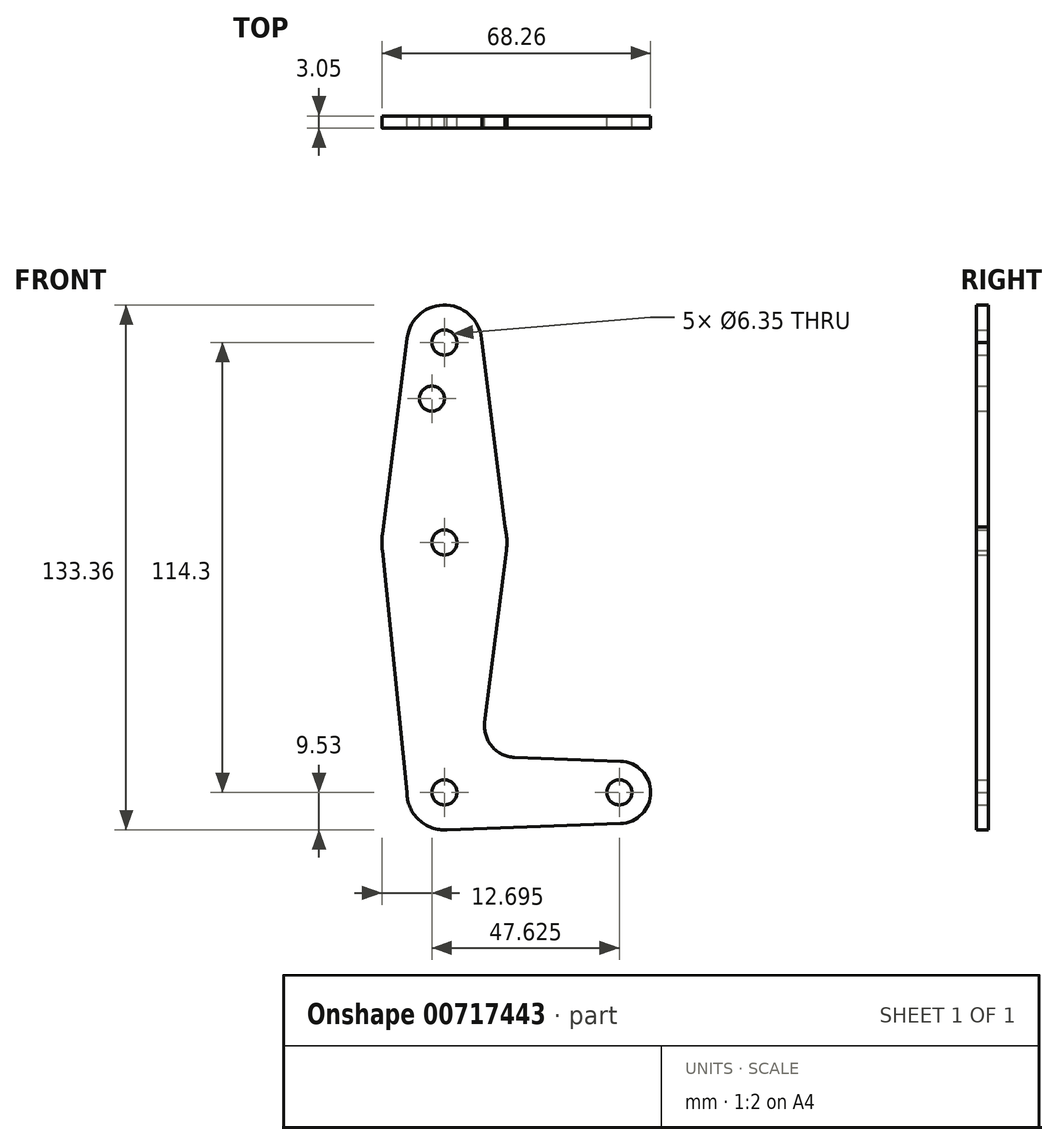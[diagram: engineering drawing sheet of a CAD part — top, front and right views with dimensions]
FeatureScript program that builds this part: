
annotation { "Feature Type Name" : "Feature", "Feature Type Description" : "" }
export const myFeature = defineFeature(function(context is Context, id is Id, definition is map)
    precondition{}
    {
        {
            var Q0;
            Q0=qCreatedBy(makeId("Front.planeOp"),FACE);
            var sketch = newSketch(context, id + "F0", { "sketchPlane" : qUnion([Q0])});
            skLineSegment(sketch, "E0", {"start": v(0, 114.3) * mm, "end": v(0, 0) * mm});
            skLineSegment(sketch, "E1", {"start": v(0, 0) * mm, "end": v(44.45, 0) * mm});
            skCircle(sketch, "E2", {"center": v(0, 114.3) * mm, "radius": 9.53 * mm});
            skCircle(sketch, "E3", {"center": v(0, 0) * mm, "radius": 9.53 * mm});
            skCircle(sketch, "E4", {"center": v(44.45, 0) * mm, "radius": 7.94 * mm});
            skCircle(sketch, "E5", {"center": v(0, 63.5) * mm, "radius": 15.88 * mm});
            skLineSegment(sketch, "E6", {"start": v(-9.45, 115.5) * mm, "end": v(-15.75, 65.48) * mm});
            skLineSegment(sketch, "E7", {"start": v(9.52, 114.3) * mm, "end": v(15.88, 63.5) * mm});
            skLineSegment(sketch, "E8", {"start": v(17.85, 8.89) * mm, "end": v(44.73, 7.93) * mm});
            skLineSegment(sketch, "E9", {"start": v(0, -9.53) * mm, "end": v(44.73, -7.93) * mm});
            skLineSegment(sketch, "E10", {"start": v(-9.52, 0) * mm, "end": v(-15.75, 61.52) * mm});
            skLineSegment(sketch, "E11", {"start": v(15.75, 61.52) * mm, "end": v(10.25, 17.83) * mm});
            skCircle(sketch, "E12", {"center": v(0, 114.3) * mm, "radius": 3.18 * mm});
            skCircle(sketch, "E13", {"center": v(0, 63.5) * mm, "radius": 3.18 * mm});
            skCircle(sketch, "E14", {"center": v(0, 0) * mm, "radius": 3.18 * mm});
            skCircle(sketch, "E15", {"center": v(44.45, 0) * mm, "radius": 3.18 * mm});
            skCircle(sketch, "E16", {"center": v(-3.17, 100.03) * mm, "radius": 3.18 * mm});
            skArc(sketch, "E17.filletArc", {"start": v(10.25, 17.83) * mm, "mid": v(12.08, 11.68) * mm, "end": v(17.85, 8.89) * mm});
            skSolve(sketch);
        }
        {
            var Q0;
            Q0 = qSketchRegion(id + "F0", true);
            var Q1;
            {var subQ0=sQuery(id+"F0.wireOp",EDGE,"E3");var subQ1=sQuery(id+"F0.wireOp",EDGE,"E0");var subQ2=makeQuery(id+"F0.imprint","INTERSECT",VERTEX,{"derivedFrom":[subQ1,subQ0]});Q1=makeQuery(id+"F0.imprint","IMPRINT",FACE,{"disambiguationData":[TD([[makeQuery(id+"F0.imprint","IMPRINT",EDGE,{"disambiguationData":[TD([[subQ2,-1.0]])],"derivedFrom":subQ1}),1.0]])]});}
            extrude(context, id + "F1", {"entities" : qUnion([Q0, Q1]), "depth" : 3.05 * mm, "offsetDistance" : 25.4 * mm});
        }
    });
